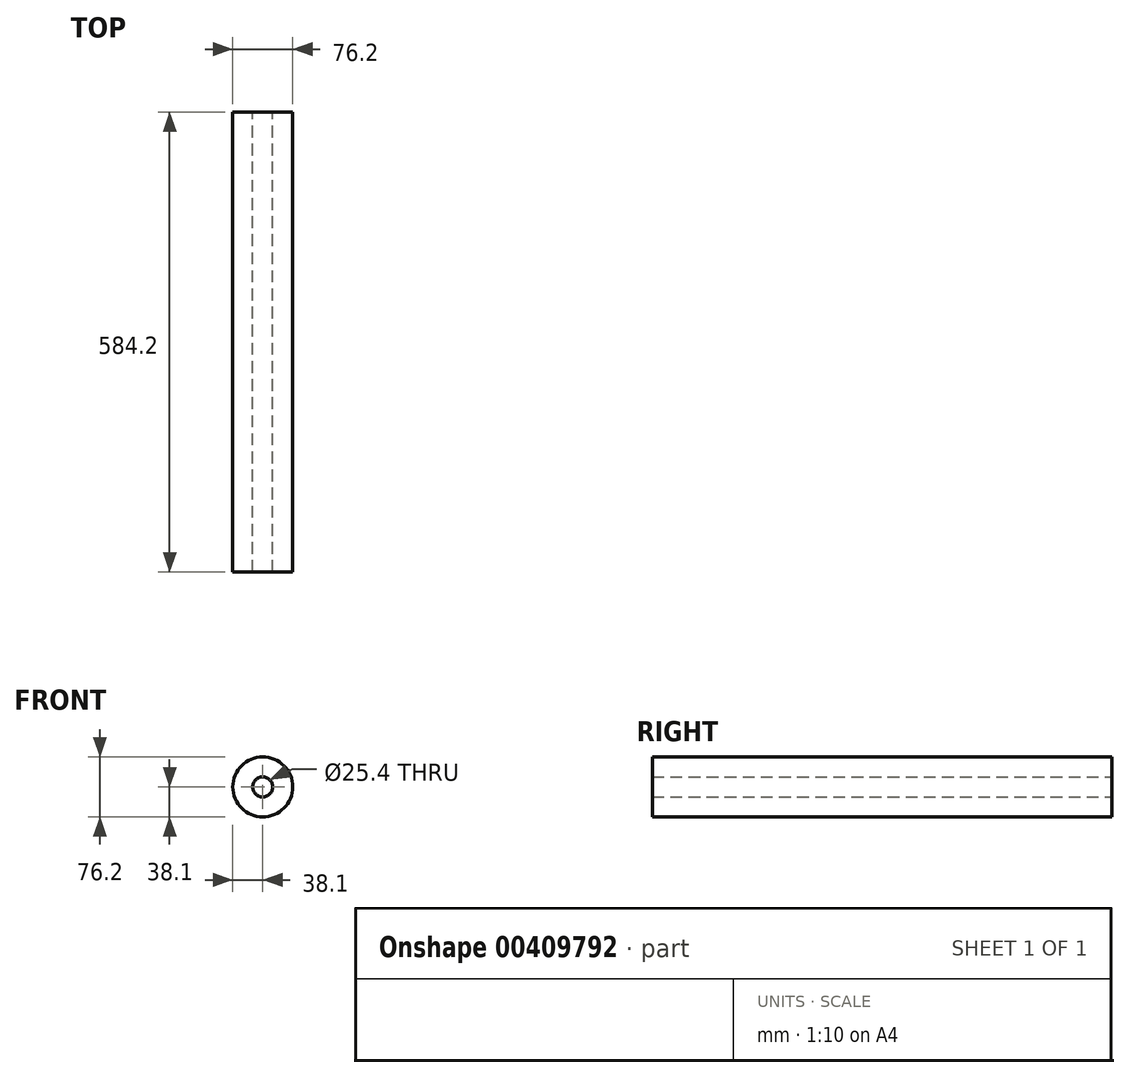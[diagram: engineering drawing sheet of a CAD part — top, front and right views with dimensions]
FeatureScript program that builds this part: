
annotation { "Feature Type Name" : "Feature", "Feature Type Description" : "" }
export const myFeature = defineFeature(function(context is Context, id is Id, definition is map)
    precondition{}
    {
        {
            var Q0;
            Q0=qCreatedBy(makeId("Front.planeOp"),FACE);
            var sketch = newSketch(context, id + "F0", { "sketchPlane" : qUnion([Q0])});
            skCircle(sketch, "E0", {"center": v(0, 0) * mm, "radius": 38.1 * mm});
            skCircle(sketch, "E1", {"center": v(0, 0) * mm, "radius": 12.7 * mm});
            skSolve(sketch);
        }
        {
            var Q0;
            Q0=makeQuery(id+"F0.imprint","IMPRINT",FACE,{"disambiguationData":[TD([[makeQuery(id+"F0.imprint","IMPRINT",EDGE,{"derivedFrom":sQuery(id+"F0.wireOp",EDGE,"E0")}),1.0]])]});
            extrude(context, id + "F1", {"entities" : qUnion([Q0]), "depth" : 584.2 * mm});
        }
        {
            var Q0;
            Q0=makeQuery(id+"F1.opExtrude","CAP_FACE",FACE,{"disambiguationData":[OSD([sQuery(id+"F0.wireOp",EDGE,"E0"),sQuery(id+"F0.wireOp",EDGE,"E1")])],"isStart":false});
            var sketch = newSketch(context, id + "F2", { "sketchPlane" : qUnion([Q0])});
            skPoint(sketch, "E2", {"position": v(0, -38.1) * mm});
            skPoint(sketch, "E3", {"position": v(-38.1, 0) * mm});
            skPoint(sketch, "E4", {"position": v(38.1, 0) * mm});
            skPoint(sketch, "E5", {"position": v(0, 38.1) * mm});
            skSolve(sketch);
        }
    });
